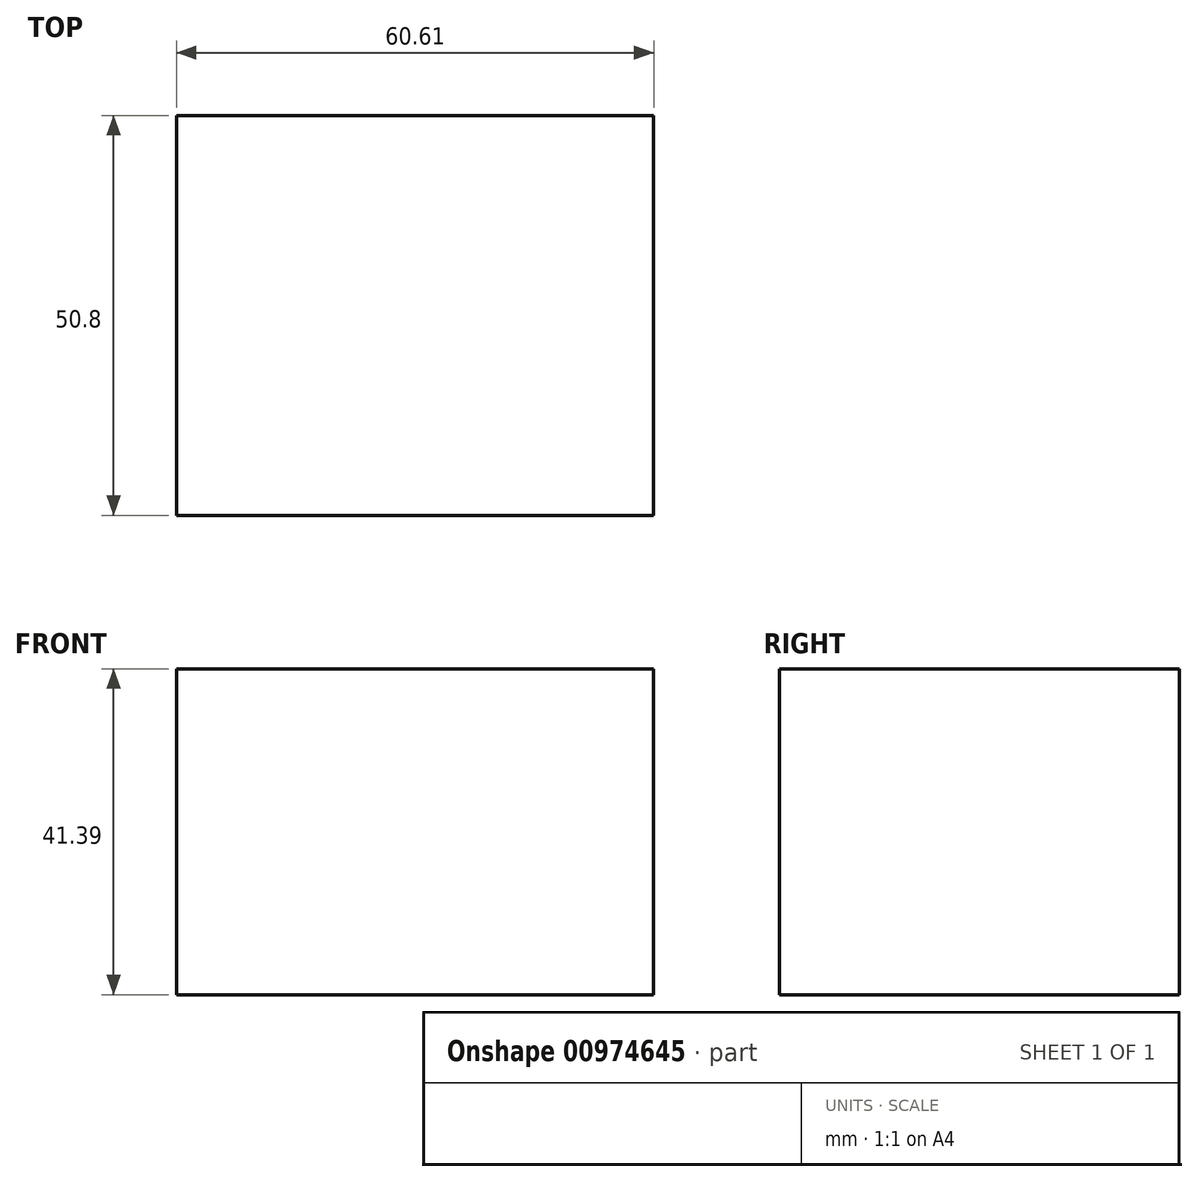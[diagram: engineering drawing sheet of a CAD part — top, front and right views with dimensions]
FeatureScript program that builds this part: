
annotation { "Feature Type Name" : "Feature", "Feature Type Description" : "" }
export const myFeature = defineFeature(function(context is Context, id is Id, definition is map)
    precondition{}
    {
        {
            var Q0;
            Q0=qCreatedBy(makeId("Front.planeOp"),FACE);
            var sketch = newSketch(context, id + "F0", { "sketchPlane" : qUnion([Q0])});
            skLineSegment(sketch, "E0", {"start": v(0, 0) * mm, "end": v(60.6, 0) * mm});
            skLineSegment(sketch, "E1", {"start": v(60.6, 0) * mm, "end": v(60.6, 41.39) * mm});
            skLineSegment(sketch, "E2", {"start": v(60.6, 41.39) * mm, "end": v(0, 41.39) * mm});
            skLineSegment(sketch, "E3", {"start": v(0, 41.39) * mm, "end": v(0, 0) * mm});
            skSolve(sketch);
        }
        {
            var Q0;
            Q0 = qSketchRegion(id + "F0", true);
            extrude(context, id + "F1", {"entities" : qUnion([Q0]), "depth" : 50.8 * mm, "offsetDistance" : 25.4 * mm});
        }
    });
